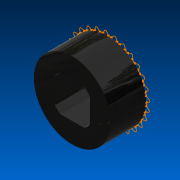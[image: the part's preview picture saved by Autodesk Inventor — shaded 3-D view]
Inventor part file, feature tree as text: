
AUTODESK INVENTOR PART (.ipt)
format: ipt  version: 2022 (Build 260153000, 153)  size: 309,248 bytes
history: native  units: in
note: dims shown in document units (in); Inventor stores cm internally (conversion verified against a paired STEP export)
features: sketch x3, other x3, extrude x2, reference x1
ambient origin geometry x8: Origin, YZ Plane, XZ Plane, XY Plane, X Axis, Y Axis, Z Axis, Center Point
bodies: Solid1 (feature_tree)
feature tree (9):
  sketch  "Sketch1"  dims[d0=0.25in d1=0.3in]
  extrude  "Extrusion1"  Depth=0.3in
  extrude  "Extrusion2"  Depth=0.5352in
  sketch  "Sketch2"  dims[d2=0.15in d3=0.5352in]
  sketch  "Sketch3"  dims[d4=0.25in d5=0.0in d6=0.2in d7=0.0in]
  reference  "Reference1"
  other  "Tracking Wheel Assembly.iam"
  other  "VersaPlanetary Integrated Encoder (217-5046):1"
  other  "217-4783-005 Rev7_40t_spur_REF_14deg_3"
